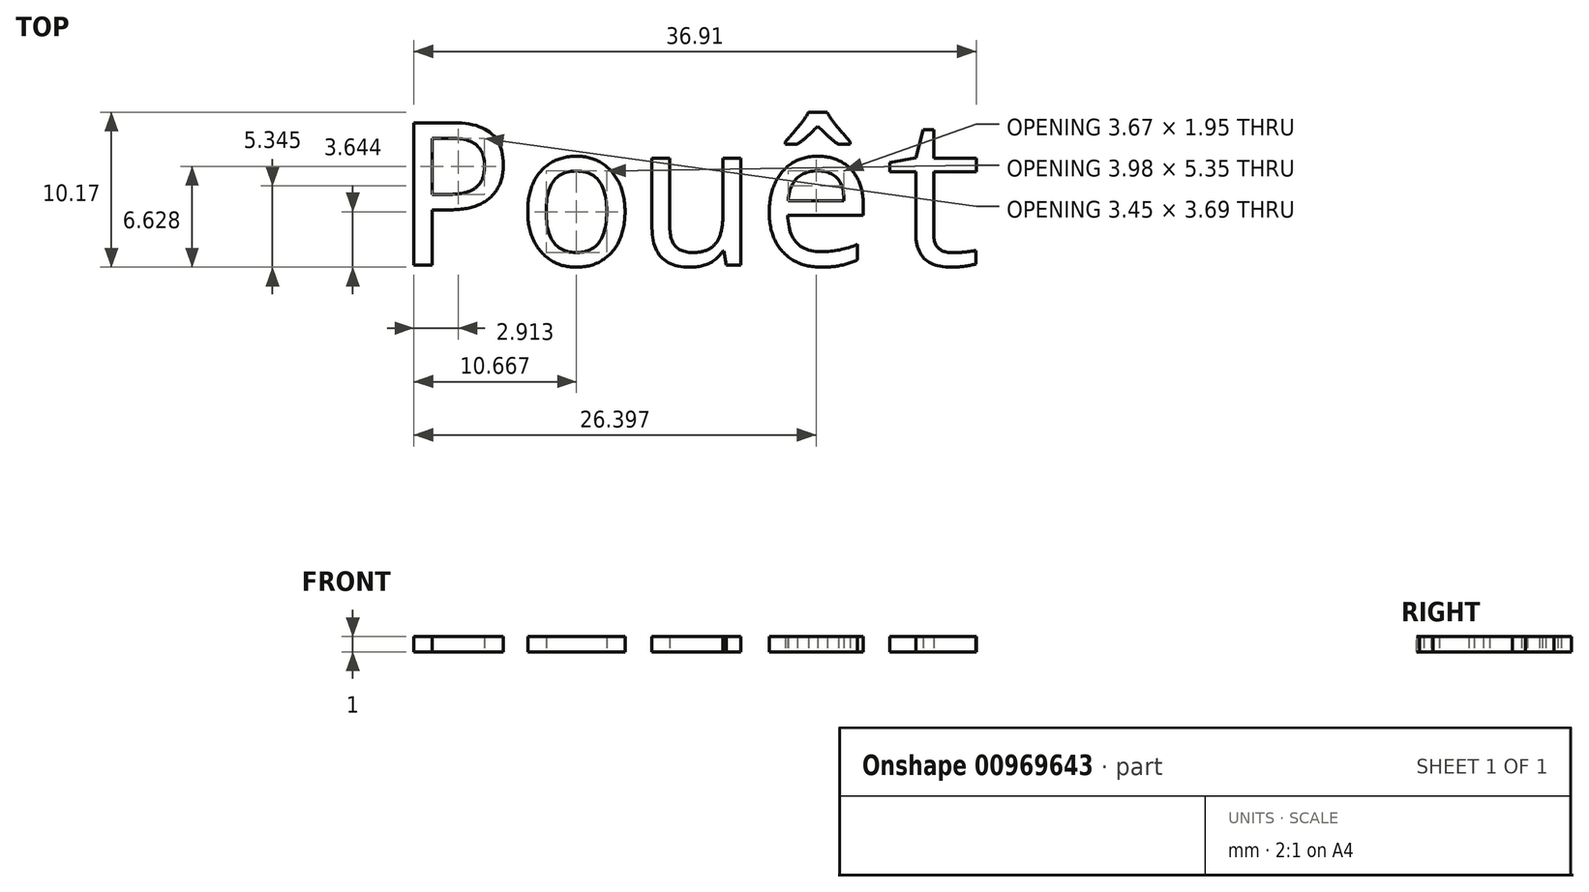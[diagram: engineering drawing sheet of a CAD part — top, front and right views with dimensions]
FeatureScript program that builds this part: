
annotation { "Feature Type Name" : "Feature", "Feature Type Description" : "" }
export const myFeature = defineFeature(function(context is Context, id is Id, definition is map)
    precondition{}
    {
        {
            var Q0;
            Q0=qCreatedBy(makeId("Top.planeOp"),FACE);
            var sketch = newSketch(context, id + "F0", { "sketchPlane" : qUnion([Q0])});
            skText(sketch, "E0", { "text": "Pouêt", "fontName": "DroidSansMono.ttf"});
            const initialGuessF0  = {"E0": [-0.01956, -0.00402, 1, 0, 0.00944]};
            skSetInitialGuess(sketch, initialGuessF0);
            skSolve(sketch);
        }
        {
            var Q0;
            Q0 = qSketchRegion(id + "F0", true);
            extrude(context, id + "F1", {"entities" : qUnion([Q0]), "depth" : 1 * mm, "offsetDistance" : 25 * mm});
        }
    });
